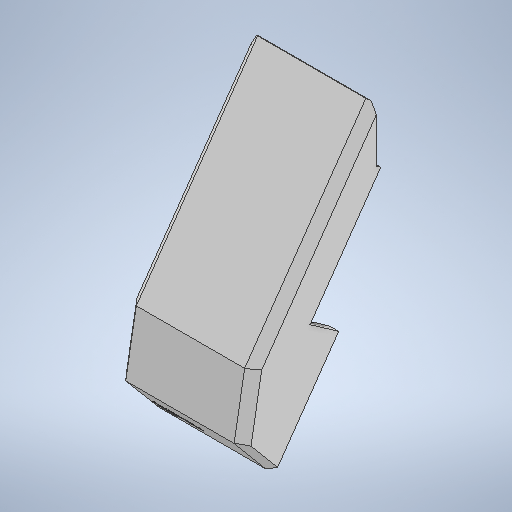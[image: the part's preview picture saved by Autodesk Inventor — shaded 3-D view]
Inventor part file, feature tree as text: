
AUTODESK INVENTOR PART (.ipt)
format: ipt  version: 2025.3 (Build 293356030, 356C)  size: 1,504,768 bytes
history: native  units: in
note: dims shown in document units (in); Inventor stores cm internally (conversion verified against a paired STEP export)
features: sketch x51, extrude x46, projected_geometry x16, plane x10, chamfer x2, move_body x1, fillet x1, thicken_offset x1, hole x1
ambient origin geometry x8: Origin, YZ Plane, XZ Plane, XY Plane, X Axis, Y Axis, Z Axis, Center Point
bodies: Solid1 (feature_tree)
feature tree (129):
  extrude  "Extrusion1"  Depth=0.1969in TaperAngle=0.0deg
  move_body  "Move Body1"
  plane  "Work Plane1"
  sketch  "Sketch5"  dims[d5=1.7717in d6=1.7717in d7=1.7717in d8=1.7717in d9=0.8108in d10=90.0deg d11=0.0787in d12=0.3701in d13=0.4252in d14=0.1362in d15=-0.0984in d16=-0.0591in d17=0.0in]
  plane  "Work Plane2"
  extrude  "Extrusion4"  TaperAngle=0.0deg  [1 undecoded]
  extrude  "Extrusion6"  Depth=0.2405in
  extrude  "Extrusion8"  Depth=2.5591in TaperAngle=0.0deg
  chamfer  "Chamfer1"  [1 undecoded]
  extrude  "Extrusion11"  Depth=0.2362in
  plane  "Work Plane3"
  plane  "Work Plane7"
  extrude  "Extrusion22"  Depth=0.1969in TaperAngle=0.0deg
  extrude  "Extrusion25"  Depth=0.5027in
  extrude  "Extrusion26"  Depth=0.5027in
  sketch  "Sketch33"  dims[d96=0.2362in d97=0.0in d100=3.6403in]
  extrude  "Extrusion27"  Depth=0.2362in TaperAngle=0.0deg
  extrude  "Extrusion28"  Depth=3.6403in
  sketch  "Sketch36"  dims[d123=0.9331in d124=0.9712in d125=0.0in]
  extrude  "Extrusion29"  Depth=1.9685in
  extrude  "Extrusion30"  Depth=0.1575in
  extrude  "Extrusion31"  Depth=0.9712in TaperAngle=0.0deg
  sketch  "Sketch39"  dims[d138=0.4331in d139=0.1181in d140=0.0in]
  extrude  "Extrusion32"  Depth=11.3469in TaperAngle=0.0deg
  fillet  "Fillet1"  Radius=11.3469in
  extrude  "Extrusion33"  Depth=0.4331in
  extrude  "Extrusion34"  Depth=0.1181in TaperAngle=0.0deg
  extrude  "Extrusion35"  Depth=0.0787in
  plane  "Work Plane8"
  sketch  "Sketch45"  dims[d160=0.1181in d161=0.0in d162=0.1969in d163=0.0in d164=0.1181in d165=0.0in]
  extrude  "Extrusion37"  Depth=0.2756in
  extrude  "Extrusion38"  Depth=0.1181in TaperAngle=0.0deg
  extrude  "Extrusion40"  Depth=0.5906in
  extrude  "Extrusion41"  Depth=0.1181in TaperAngle=0.0deg
  extrude  "Extrusion43"  Depth=4.7244in TaperAngle=0.0deg
  extrude  "Extrusion44"  Depth=0.7313in TaperAngle=0.0deg
  extrude  "Extrusion46"  TaperAngle=0.0deg  [1 undecoded]
  extrude  "Extrusion48"  Depth=1.1024in
  extrude  "Extrusion50"  Depth=0.0394in TaperAngle=0.0deg
  extrude  "Extrusion51"  Depth=5.8937in TaperAngle=0.0deg
  extrude  "Extrusion53"  Depth=2.3622in TaperAngle=0.0deg
  plane  "Work Plane9"
  plane  "Work Plane12"
  extrude  "Extrusion65"  Depth=0.1969in
  plane  "Work Plane13"
  extrude  "Extrusion67"  TaperAngle=60.0deg  [1 undecoded]
  plane  "Work Plane14"
  extrude  "Extrusion68"  Depth=0.7902in
  extrude  "Extrusion69"  Depth=0.3436in
  extrude  "Extrusion70"  Depth=0.2362in
  sketch  "Sketch84"  dims[d298=0.2362in d299=0.0in d300=0.2362in d301=0.0in]
  extrude  "Extrusion71"  TaperAngle=0.0deg  [1 undecoded]
  extrude  "Extrusion72"  Depth=0.2362in TaperAngle=0.0deg
  extrude  "Extrusion73"  TaperAngle=90.0deg  [1 undecoded]
  extrude  "Extrusion74"  Depth=0.2362in TaperAngle=0.0deg
  extrude  "Extrusion76"  Depth=0.0787in
  thicken_offset  "Thicken1"
  extrude  "Extrusion78"  Depth=0.1181in TaperAngle=0.0deg
  plane  "Work Plane15"
  extrude  "Extrusion79"  Depth=0.0787in
  extrude  "Extrusion80"  Depth=0.0787in
  extrude  "Extrusion81"  Depth=0.0787in
  extrude  "Extrusion82"  TaperAngle=0.0deg  [1 undecoded]
  extrude  "Extrusion83"  TaperAngle=0.0deg  [1 undecoded]
  chamfer  "Chamfer3"  Distance=0.137in
  extrude  "Extrusion84"  Depth=0.3937in
  extrude  "Extrusion85"  Depth=0.0787in TaperAngle=0.0deg
  sketch  "Sketch1"  dims[d1=0.5512in d2=0.1969in d3=0.0in]
  sketch  "Sketch6"  dims[d18=0.2749in d24=0.2405in]
  sketch  "Sketch8"  dims[d25=2.7559in d26=0.0in d29=2.5591in d30=0.0in d36=0.0in d37=0.0in]
  sketch  "Sketch12"  dims[d42=0.2362in d43=0.2362in]
  sketch  "Sketch15"  dims[d52=0.2362in d53=0.0787in d54=45.0deg d55=0.1969in d56=0.0in]
  sketch  "Sketch28"  dims[d76=0.5027in d77=0.5027in]
  sketch  "Sketch31"  dims[d78=0.5027in d79=0.5027in]
  sketch  "Sketch32"  dims[d83=0.0in d84=0.0in d94=0.2362in d95=0.0in]
  sketch  "Sketch34"  dims[d101=2.7717in d112=1.9685in]
  sketch  "Sketch35"  dims[d113=0.6299in d114=0.0in d115=0.1575in d117=0.1575in d121=1.9685in d122=0.7874in]
  sketch  "Sketch37"  dims[d126=0.5906in d127=0.0in d128=11.3469in d129=0.0in d130=11.3469in d131=0.0in]
  sketch  "Sketch38"  dims[d136=0.4331in d137=0.4331in]
  sketch  "Sketch40"  dims[d141=0.6299in d142=0.0787in]
  sketch  "Sketch41"  dims[d147=0.2756in d149=0.2756in]
  sketch  "Sketch42"  dims[d150=0.0in d151=0.0in d154=0.1181in d155=0.0in]
  sketch  "Sketch44"  dims[d156=0.1181in d157=0.0in d158=0.5906in]
  projected_geometry  "Projected Loop2"
  projected_geometry  "Projected Loop3"
  projected_geometry  "Projected Loop5"
  sketch  "Sketch47"  dims[d168=0.5906in d169=0.0in d170=4.7244in d171=0.0in]
  sketch  "Sketch49"  dims[d174=0.0in d175=0.0in d176=0.7313in d177=0.0in]
  sketch  "Sketch50"  dims[d186=0.0in d187=0.0in d188=0.0in d189=0.0in]
  sketch  "Sketch52"  dims[d194=0.0in d195=0.0in d196=1.1024in]
  sketch  "Sketch53"  dims[d197=0.5906in d200=0.0394in d201=0.0in]
  sketch  "Sketch56"  dims[d218=0.0in d219=0.0in d220=5.8937in d221=0.0in]
  sketch  "Sketch59"  dims[d233=0.9963in d234=2.3622in d235=0.0in]
  sketch  "Sketch60"  dims[d266=0.1378in d268=0.1969in]
  sketch  "Sketch61"  dims[d269=0.1378in d270=60.0deg]
  sketch  "Sketch63"  dims[d271=4.5565in d272=0.0in d277=0.7902in]
  projected_geometry  "Projected Loop8"
  sketch  "Sketch76"  dims[d278=0.5906in d279=1.378in d280=0.0in d281=0.0in d282=0.3436in]
  sketch  "Sketch78"  dims[d283=1.378in d284=0.9843in d285=0.0in d286=0.0in d287=0.2362in]
  projected_geometry  "Projected Loop14"
  sketch  "Sketch79"  dims[d288=0.0in d289=0.0in d290=0.0in d291=0.0in]
  projected_geometry  "Projected Loop15"
  projected_geometry  "Projected Loop16"
  projected_geometry  "Projected Loop17"
  sketch  "Sketch80"  dims[d292=0.5894in d293=0.2362in d294=0.0in]
  projected_geometry  "Projected Loop18"
  projected_geometry  "Projected Loop20"
  sketch  "Sketch83"  dims[d295=0.2362in d296=0.0in d297=90.0deg]
  projected_geometry  "Projected Loop22"
  sketch  "Sketch85"  dims[d304=0.0in d305=0.0in d306=0.0787in]
  sketch  "Sketch86"  dims[d307=0.0787in d314=0.1181in d315=0.0in]
  sketch  "Sketch87"  dims[d316=90.0deg d317=0.0787in]
  sketch  "Sketch88"  dims[d318=0.0787in d319=0.0787in]
  sketch  "Sketch90"  dims[d320=1.7037in d321=0.0in d322=0.0787in]
  projected_geometry  "Projected Loop23"
  sketch  "Sketch92"  dims[d323=0.0in d324=0.0in d325=0.0in d326=0.0in]
  projected_geometry  "Projected Loop25"
  projected_geometry  "Projected Loop26"
  sketch  "Sketch94"  dims[d327=0.137in d328=0.0in d329=0.0in d330=0.137in d331=0.0in]
  sketch  "Sketch95"  dims[d332=0.1181in d333=0.0787in d334=45.0deg d335=0.3937in]
  sketch  "Sketch96"  dims[d336=0.137in d337=0.0in d339=0.0787in d340=0.0in]
  sketch  "Sketch97"  dims[d38=0.0197in d39=0.0344in]
  sketch  "Sketch98"  dims[d57=0.0197in]
  projected_geometry  "Projected Loop30"
  projected_geometry  "Projected Loop31"
  sketch  "Sketch99"  dims[d58=0.0344in]
  sketch  "Sketch100"  dims[d59=0.0197in d60=0.0344in d81=0.0197in d82=0.0344in d159=0.0344in d178=0.0in d179=0.0in d180=0.0in d181=0.0in d202=0.0197in d203=0.0344in d222=0.0197in d223=0.0344in]
  sketch  "Sketch2"  dims[d4=0.315in]
  hole  "Hole1"  [1 undecoded]
note: 9 required parameter values undecoded (feature->parameter linkage not recoverable at this tier; creation-order binding heuristic only, values carry confidence <= 0.55)
